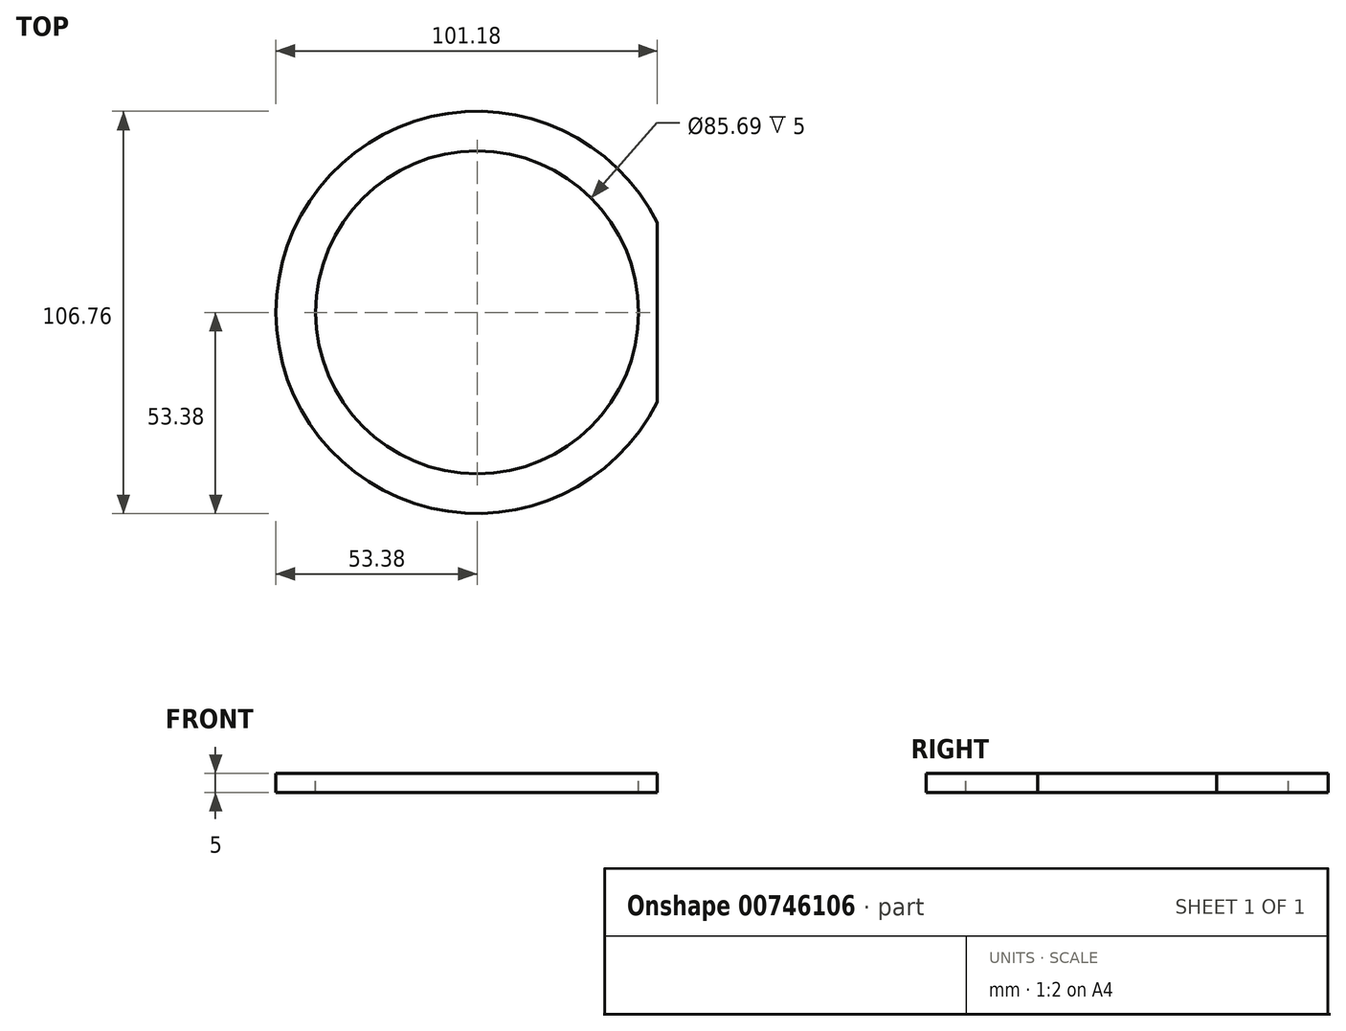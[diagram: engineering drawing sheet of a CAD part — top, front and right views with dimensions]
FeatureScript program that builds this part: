
annotation { "Feature Type Name" : "Feature", "Feature Type Description" : "" }
export const myFeature = defineFeature(function(context is Context, id is Id, definition is map)
    precondition{}
    {
        {
            var Q0;
            Q0=qCreatedBy(makeId("Top.planeOp"),FACE);
            var sketch = newSketch(context, id + "F0", { "sketchPlane" : qUnion([Q0])});
            skCircle(sketch, "E0", {"center": v(0, 0) * mm, "radius": 53.38 * mm});
            skSolve(sketch);
        }
        {
            var Q0;
            Q0=makeQuery(id+"F0.imprint","IMPRINT",FACE,{"disambiguationData":[TD([[makeQuery(id+"F0.imprint","IMPRINT",EDGE,{"derivedFrom":sQuery(id+"F0.wireOp",EDGE,"E0")}),1.0]])]});
            extrude(context, id + "F1", {"entities" : qUnion([Q0]), "depth" : 5 * mm, "offsetDistance" : 25.4 * mm});
        }
        {
            var Q0;
            Q0=makeQuery(id+"F1.opExtrude","CAP_FACE",FACE,{"disambiguationData":[OSD([sQuery(id+"F0.wireOp",EDGE,"E0")])],"isStart":false});
            var sketch = newSketch(context, id + "F2", { "sketchPlane" : qUnion([Q0])});
            skCircle(sketch, "E1", {"center": v(0, 0) * mm, "radius": 42.84 * mm});
            skSolve(sketch);
        }
        {
            var Q0;
            Q0=makeQuery(id+"F2.imprint","IMPRINT",FACE,{"disambiguationData":[TD([[makeQuery(id+"F2.imprint","IMPRINT",EDGE,{"derivedFrom":sQuery(id+"F2.wireOp",EDGE,"E1")}),1.0]])]});
            extrude(context, id + "F3", {"entities" : qUnion([Q0]), "operationType" : NewBodyOperationType.REMOVE, "oppositeDirection" : true, "depth" : 5 * mm, "offsetDistance" : 25.4 * mm});
        }
        {
            var Q0;
            Q0=qCreatedBy(makeId("Top.planeOp"),FACE);
            var sketch = newSketch(context, id + "F4", { "sketchPlane" : qUnion([Q0])});
            skLineSegment(sketch, "E2.bottom", {"start": v(47.8, 53.61) * mm, "end": v(58.73, 53.61) * mm});
            skLineSegment(sketch, "E2.top", {"start": v(47.8, -53.15) * mm, "end": v(58.73, -53.15) * mm});
            skLineSegment(sketch, "E2.left", {"start": v(47.8, 53.61) * mm, "end": v(47.8, -53.15) * mm});
            skLineSegment(sketch, "E2.right", {"start": v(58.73, 53.61) * mm, "end": v(58.73, -53.15) * mm});
            skSolve(sketch);
        }
        {
            var Q0;
            Q0=makeQuery(id+"F4.imprint","IMPRINT",FACE,{"disambiguationData":[TD([[makeQuery(id+"F4.imprint","IMPRINT",EDGE,{"derivedFrom":sQuery(id+"F4.wireOp",EDGE,"E2.bottom")}),-1.0]])]});
            extrude(context, id + "F5", {"entities" : qUnion([Q0]), "operationType" : NewBodyOperationType.ADD, "depth" : 25.4 * mm, "offsetDistance" : 25.4 * mm});
        }
        {
            var Q0;
            Q0=makeQuery(id+"F5.opExtrude","CAP_FACE",FACE,{"disambiguationData":[OSD([sQuery(id+"F4.wireOp",EDGE,"E2.bottom"),sQuery(id+"F4.wireOp",EDGE,"E2.top"),sQuery(id+"F4.wireOp",EDGE,"E2.left"),sQuery(id+"F4.wireOp",EDGE,"E2.right")])],"isStart":false});
            extrude(context, id + "F6", {"entities" : qUnion([Q0]), "operationType" : NewBodyOperationType.REMOVE, "oppositeDirection" : true, "depth" : 25.4 * mm, "offsetDistance" : 25.4 * mm});
        }
    });
